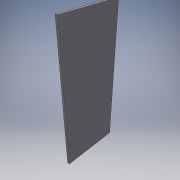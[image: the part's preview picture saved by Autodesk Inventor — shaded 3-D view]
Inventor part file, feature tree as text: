
AUTODESK INVENTOR PART (.ipt)
format: ipt  version: 2016 (Build 200138000, 138)  size: 88,064 bytes
history: native  units: in
note: dims shown in document units (in); Inventor stores cm internally (conversion verified against a paired STEP export)
features: extrude x1, sketch x1
ambient origin geometry x8: Origin, YZ Plane, XZ Plane, XY Plane, X Axis, Y Axis, Z Axis, Center Point
bodies: Solid1 (feature_tree)
feature tree (2):
  extrude  "Extrusion1"  Depth=44.0in
  sketch  "Sketch1"  dims[d0=18.0in d1=44.0in d2=0.75in d3=0.0in]
